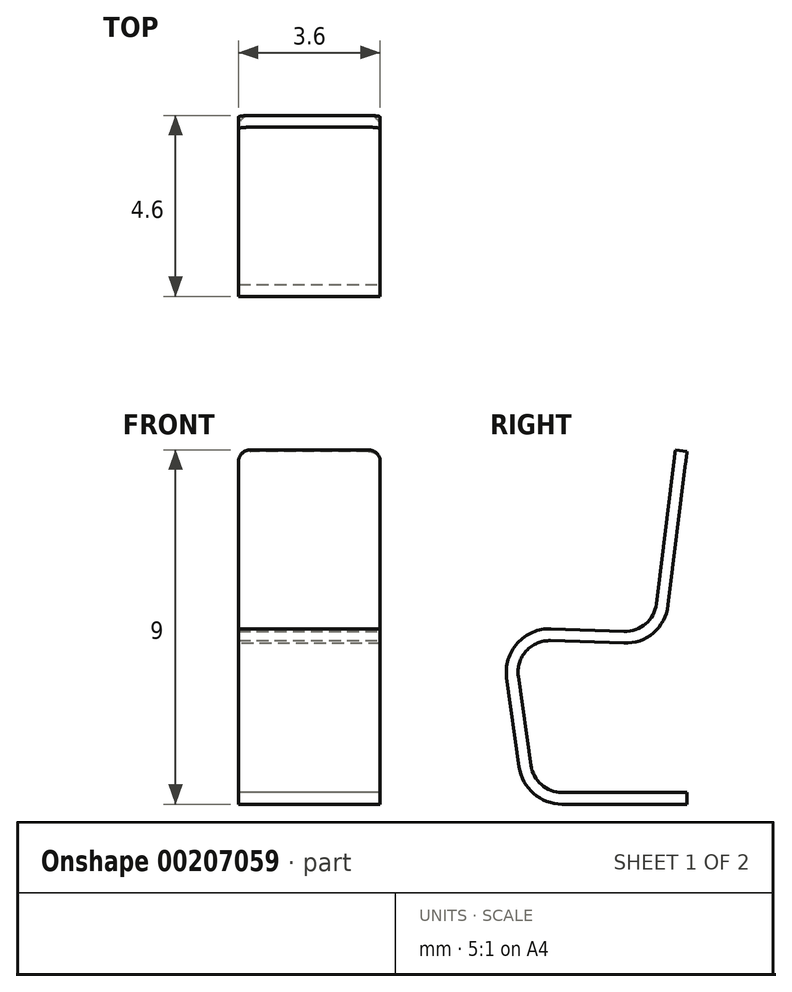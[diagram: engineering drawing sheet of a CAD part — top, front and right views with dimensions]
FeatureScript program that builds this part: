
annotation { "Feature Type Name" : "Feature", "Feature Type Description" : "" }
export const myFeature = defineFeature(function(context is Context, id is Id, definition is map)
    precondition{}
    {
        {
            var Q0;
            Q0=qCreatedBy(makeId("Right.planeOp"),FACE);
            var sketch = newSketch(context, id + "F0", { "sketchPlane" : qUnion([Q0])});
            skLineSegment(sketch, "E0", {"start": v(2.07, 0) * mm, "end": v(-2.07, 0) * mm});
            skLineSegment(sketch, "E1", {"start": v(-2.07, 0) * mm, "end": v(-2.7, 4.5) * mm});
            skLineSegment(sketch, "E2", {"start": v(-2.7, 4.5) * mm, "end": v(1.2, 4.36) * mm});
            skLineSegment(sketch, "E3", {"start": v(1.2, 4.36) * mm, "end": v(1.77, 9) * mm});
            skLineSegment(sketch, "E4", {"start": v(1.77, 9) * mm, "end": v(2.07, 8.96) * mm});
            skLineSegment(sketch, "E5", {"start": v(2.07, 8.96) * mm, "end": v(1.46, 4.05) * mm});
            skLineSegment(sketch, "E6", {"start": v(1.46, 4.05) * mm, "end": v(-2.35, 4.19) * mm});
            skLineSegment(sketch, "E7", {"start": v(-2.35, 4.19) * mm, "end": v(-1.8, 0.3) * mm});
            skLineSegment(sketch, "E8", {"start": v(-1.8, 0.3) * mm, "end": v(2.07, 0.3) * mm});
            skLineSegment(sketch, "E9", {"start": v(2.07, 0.3) * mm, "end": v(2.07, 0) * mm});
            skLineSegment(sketch, "E10", {"start": v(-2.7, 4.5) * mm, "end": v(4.96, 4.5) * mm, "construction": true});
            skSolve(sketch);
        }
        {
            var Q0;
            Q0=makeQuery(id+"F0.imprint","IMPRINT",FACE,{"disambiguationData":[TD([[makeQuery(id+"F0.imprint","IMPRINT",EDGE,{"derivedFrom":sQuery(id+"F0.wireOp",EDGE,"E0")}),-1.0]])]});
            extrude(context, id + "F1", {"entities" : qUnion([Q0]), "depth" : 3.6 * mm, "offsetDistance" : 25 * mm});
        }
        {
            var Q0;
            Q0=makeQuery(id+"F1.opExtrude","SWEPT_EDGE",EDGE,{"disambiguationData":[OSD([sQuery(id+"F0.wireOp",EDGE,"E6"),sQuery(id+"F0.wireOp",EDGE,"E7")])]});
            var Q1;
            Q1=makeQuery(id+"F1.opExtrude","SWEPT_EDGE",EDGE,{"disambiguationData":[OSD([sQuery(id+"F0.wireOp",EDGE,"E7"),sQuery(id+"F0.wireOp",EDGE,"E8")])]});
            var Q2;
            Q2=makeQuery(id+"F1.opExtrude","SWEPT_EDGE",EDGE,{"disambiguationData":[OSD([sQuery(id+"F0.wireOp",EDGE,"E2"),sQuery(id+"F0.wireOp",EDGE,"E3")])]});
            fillet(context, id + "F2", {"entities" : qUnion([Q0, Q1, Q2]), "tangentPropagation" : true, "radius" : 0.8 * mm, "defaultsChanged" : false, "vertexSettings" : [], "allowEdgeOverflow" : false});
        }
        {
            var Q0;
            Q0=makeQuery(id+"F1.opExtrude","SWEPT_EDGE",EDGE,{"disambiguationData":[OSD([sQuery(id+"F0.wireOp",EDGE,"E1"),sQuery(id+"F0.wireOp",EDGE,"E2")])]});
            var Q1;
            Q1=makeQuery(id+"F1.opExtrude","SWEPT_EDGE",EDGE,{"disambiguationData":[OSD([sQuery(id+"F0.wireOp",EDGE,"E5"),sQuery(id+"F0.wireOp",EDGE,"E6")])]});
            var Q2;
            Q2=makeQuery(id+"F1.opExtrude","SWEPT_EDGE",EDGE,{"disambiguationData":[OSD([sQuery(id+"F0.wireOp",EDGE,"E0"),sQuery(id+"F0.wireOp",EDGE,"E1")])]});
            fillet(context, id + "F3", {"entities" : qUnion([Q0, Q1, Q2]), "tangentPropagation" : true, "radius" : 1.1 * mm, "defaultsChanged" : false, "vertexSettings" : [], "allowEdgeOverflow" : false});
        }
        {
            var Q0;
            Q0=makeQuery(id+"F1.opExtrude","CAP_EDGE",EDGE,{"disambiguationData":[OSD([sQuery(id+"F0.wireOp",EDGE,"E4")])],"isStart":false});
            var Q1;
            Q1=makeQuery(id+"F1.opExtrude","CAP_EDGE",EDGE,{"disambiguationData":[OSD([sQuery(id+"F0.wireOp",EDGE,"E4")])],"isStart":true});
            var Q2;
            Q2=makeQuery(id+"F1.opExtrude","CAP_EDGE",EDGE,{"disambiguationData":[OSD([sQuery(id+"F0.wireOp",EDGE,"E9")])],"isStart":false});
            var Q3;
            Q3=makeQuery(id+"F1.opExtrude","CAP_EDGE",EDGE,{"disambiguationData":[OSD([sQuery(id+"F0.wireOp",EDGE,"E9")])],"isStart":true});
            fillet(context, id + "F4", {"entities" : qUnion([Q0, Q1, Q2, Q3]), "tangentPropagation" : true, "radius" : 0.3 * mm, "defaultsChanged" : true, "vertexSettings" : [], "allowEdgeOverflow" : false});
        }
    });
